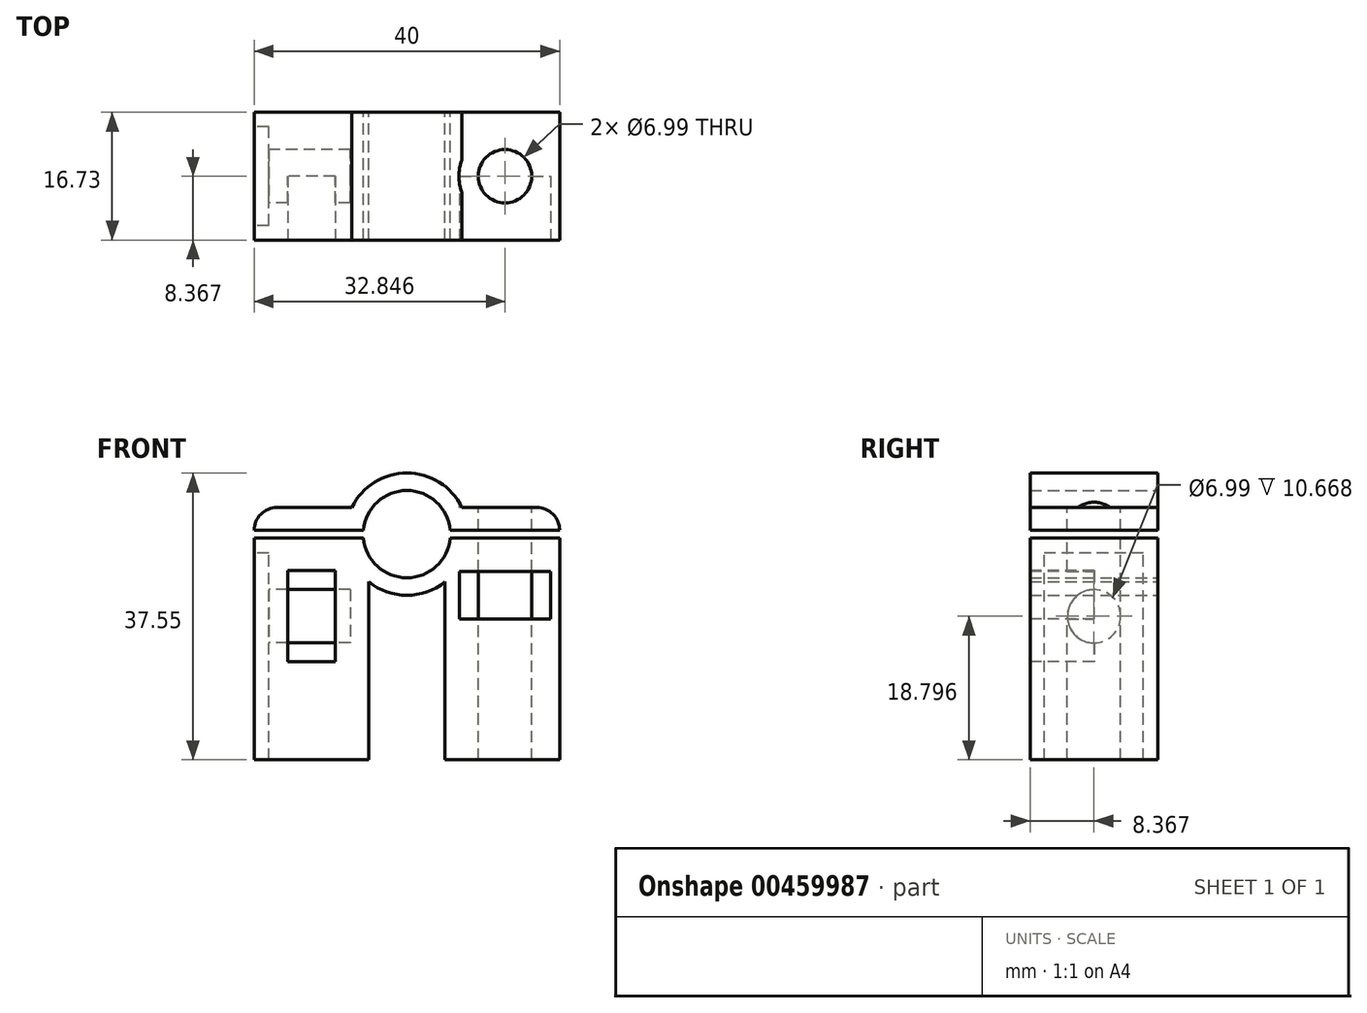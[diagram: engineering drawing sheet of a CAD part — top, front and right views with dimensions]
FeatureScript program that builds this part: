
annotation { "Feature Type Name" : "Feature", "Feature Type Description" : "" }
export const myFeature = defineFeature(function(context is Context, id is Id, definition is map)
    precondition{}
    {
        {
            var Q0;
            Q0=qCreatedBy(makeId("Front.planeOp"),FACE);
            var sketch = newSketch(context, id + "F0", { "sketchPlane" : qUnion([Q0])});
            skLineSegment(sketch, "E0.bottom", {"start": v(0, 0) * mm, "end": v(-40, 0) * mm, "construction": true});
            skLineSegment(sketch, "E0.top", {"start": v(0, 29.05) * mm, "end": v(-40, 29.05) * mm, "construction": true});
            skLineSegment(sketch, "E0.left", {"start": v(0, 0) * mm, "end": v(0, 29.05) * mm});
            skLineSegment(sketch, "E0.right", {"start": v(-40, 0) * mm, "end": v(-40, 29.05) * mm});
            skArc(sketch, "E1", {"start": v(-25.7, 29.05) * mm, "mid": v(-20, 23.84) * mm, "end": v(-14.3, 29.05) * mm});
            skLineSegment(sketch, "E2", {"start": v(-25.7, 29.05) * mm, "end": v(-40, 29.05) * mm});
            skLineSegment(sketch, "E3", {"start": v(-14.3, 29.05) * mm, "end": v(0, 29.05) * mm});
            skLineSegment(sketch, "E4.bottom", {"start": v(-40, 30.05) * mm, "end": v(0, 30.05) * mm, "construction": true});
            skArc(sketch, "E5", {"start": v(-14.3, 30.05) * mm, "mid": v(-20, 35.27) * mm, "end": v(-25.7, 30.05) * mm});
            skLineSegment(sketch, "E6", {"start": v(-40, 30.05) * mm, "end": v(-25.7, 30.05) * mm});
            skLineSegment(sketch, "E7", {"start": v(-14.3, 30.05) * mm, "end": v(0, 30.05) * mm});
            skLineSegment(sketch, "E8", {"start": v(-40, 30.05) * mm, "end": v(-40, 33.05) * mm});
            skLineSegment(sketch, "E9", {"start": v(-40, 33.05) * mm, "end": v(-27.2, 33.05) * mm});
            skLineSegment(sketch, "E10", {"start": v(0, 30.05) * mm, "end": v(0, 33.05) * mm});
            skLineSegment(sketch, "E11", {"start": v(0, 33.05) * mm, "end": v(-12.8, 33.05) * mm});
            skArc(sketch, "E12", {"start": v(-12.8, 33.05) * mm, "mid": v(-20, 37.55) * mm, "end": v(-27.2, 33.05) * mm});
            skArc(sketch, "E13", {"start": v(-25, 23.3) * mm, "mid": v(-20, 21.55) * mm, "end": v(-15, 23.3) * mm});
            skLineSegment(sketch, "E14", {"start": v(-25, 23.3) * mm, "end": v(-25, 0) * mm});
            skLineSegment(sketch, "E15", {"start": v(-15, 23.3) * mm, "end": v(-15, 0) * mm});
            skLineSegment(sketch, "E16", {"start": v(-25, 0) * mm, "end": v(-40, 0) * mm});
            skLineSegment(sketch, "E17", {"start": v(-15, 0) * mm, "end": v(0, 0) * mm});
            skSolve(sketch);
        }
        {
            var Q0;
            Q0 = qSketchRegion(id + "F0", true);
            extrude(context, id + "F1", {"entities" : qUnion([Q0]), "depth" : 12.73 * mm + 4 * mm});
        }
        {
            var Q0;
            Q0=makeQuery(id+"F1.opExtrude","SWEPT_FACE",FACE,{"disambiguationData":[OSD([sQuery(id+"F0.wireOp",EDGE,"E0.right")])]});
            var sketch = newSketch(context, id + "F2", { "sketchPlane" : qUnion([Q0])});
            skLineSegment(sketch, "E18.bottom", {"start": v(1.89, 0) * mm, "end": v(14.84, 0) * mm});
            skLineSegment(sketch, "E18.top", {"start": v(1.89, 27.05) * mm, "end": v(14.84, 27.05) * mm});
            skLineSegment(sketch, "E18.left", {"start": v(1.89, 0) * mm, "end": v(1.89, 27.05) * mm});
            skLineSegment(sketch, "E18.right", {"start": v(14.84, 0) * mm, "end": v(14.84, 27.05) * mm});
            skPoint(sketch, "E19", {"position": v(8.36, 27.05) * mm});
            skPoint(sketch, "E20", {"position": v(8.36, 29.05) * mm});
            skSolve(sketch);
        }
        {
            var Q0;
            Q0 = qSketchRegion(id + "F2", true);
            extrude(context, id + "F3", {"entities" : qUnion([Q0]), "operationType" : NewBodyOperationType.REMOVE, "oppositeDirection" : true, "depth" : 1.9 * mm});
        }
        {
            var Q0;
            Q0=makeQuery(id+"F3.boolean.opBoolean","COPY",FACE,{"derivedFrom":makeQuery(id+"F3.opExtrude","CAP_FACE",FACE,{"disambiguationData":[OSD([sQuery(id+"F2.wireOp",EDGE,"E18.bottom"),sQuery(id+"F2.wireOp",EDGE,"E18.top"),sQuery(id+"F2.wireOp",EDGE,"E18.left"),sQuery(id+"F2.wireOp",EDGE,"E18.right")])],"isStart":false})});
            var sketch = newSketch(context, id + "F4", { "sketchPlane" : qUnion([Q0])});
            skLineSegment(sketch, "E21", {"start": v(8.36, 0) * mm, "end": v(8.36, 27.05) * mm, "construction": true});
            skCircle(sketch, "E22", {"center": v(8.36, 18.8) * mm, "radius": 3.5 * mm});
            skSolve(sketch);
        }
        {
            var Q0;
            Q0 = qSketchRegion(id + "F4", true);
            extrude(context, id + "F5", {"entities" : qUnion([Q0]), "operationType" : NewBodyOperationType.REMOVE, "oppositeDirection" : true, "depth" : 10.67 * mm});
        }
        {
            var Q0;
            Q0=makeQuery(id+"F1.opExtrude","SWEPT_EDGE",EDGE,{"disambiguationData":[OSD([sQuery(id+"F0.wireOp",EDGE,"E8"),sQuery(id+"F0.wireOp",EDGE,"E9")])]});
            var Q1;
            Q1=makeQuery(id+"F1.opExtrude","SWEPT_EDGE",EDGE,{"disambiguationData":[OSD([sQuery(id+"F0.wireOp",EDGE,"E10"),sQuery(id+"F0.wireOp",EDGE,"E11")])]});
            fillet(context, id + "F6", {"entities" : qUnion([Q0, Q1]), "radius" : 3 * mm, "tangentPropagation" : true, "allowEdgeOverflow" : false});
        }
        {
            var Q0;
            Q0=makeQuery(id+"F1.opExtrude","SWEPT_FACE",FACE,{"disambiguationData":[OSD([sQuery(id+"F0.wireOp",EDGE,"E11")])]});
            var sketch = newSketch(context, id + "F7", { "sketchPlane" : qUnion([Q0])});
            skCircle(sketch, "E23", {"center": v(-7.15, -8.36) * mm, "radius": 3.5 * mm});
            skLineSegment(sketch, "E24", {"start": v(0, 0) * mm, "end": v(-14.3, 0) * mm, "construction": true});
            skPoint(sketch, "E25", {"position": v(-7.15, 0) * mm});
            skLineSegment(sketch, "E26", {"start": v(-7.15, 0) * mm, "end": v(-7.9, -16.73) * mm, "construction": true});
            skSolve(sketch);
        }
        {
            var Q0;
            Q0 = qSketchRegion(id + "F7", true);
            extrude(context, id + "F8", {"entities" : qUnion([Q0]), "operationType" : NewBodyOperationType.REMOVE, "endBound" : BoundingType.THROUGH_ALL, "oppositeDirection" : true, "depth" : 19.05 * mm});
        }
        {
            var Q0;
            Q0=makeQuery(id+"F1.opExtrude","SWEPT_FACE",FACE,{"disambiguationData":[OSD([sQuery(id+"F0.wireOp",EDGE,"E3")])]});
            var sketch = newSketch(context, id + "F9", { "sketchPlane" : qUnion([Q0])});
            skCircle(sketch, "E27", {"center": v(-7.15, -8.36) * mm, "radius": 3.5 * mm});
            skSolve(sketch);
        }
        {
            var Q0;
            Q0 = qSketchRegion(id + "F9", true);
            extrude(context, id + "F10", {"entities" : qUnion([Q0]), "operationType" : NewBodyOperationType.REMOVE, "oppositeDirection" : true, "depth" : 13 * mm});
        }
        {
            var Q0;
            Q0=makeQuery(id+"F1.opExtrude","CAP_FACE",FACE,{"disambiguationData":[OSD([sQuery(id+"F0.wireOp",EDGE,"E0.left"),sQuery(id+"F0.wireOp",EDGE,"E0.right"),sQuery(id+"F0.wireOp",EDGE,"E1"),sQuery(id+"F0.wireOp",EDGE,"E2"),sQuery(id+"F0.wireOp",EDGE,"E3"),sQuery(id+"F0.wireOp",EDGE,"E13"),sQuery(id+"F0.wireOp",EDGE,"E14"),sQuery(id+"F0.wireOp",EDGE,"E15"),sQuery(id+"F0.wireOp",EDGE,"E16"),sQuery(id+"F0.wireOp",EDGE,"E17")])],"isStart":false});
            var sketch = newSketch(context, id + "F11", { "sketchPlane" : qUnion([Q0])});
            skLineSegment(sketch, "E28.bottom", {"start": v(-35.61, 24.77) * mm, "end": v(-29.39, 24.77) * mm});
            skLineSegment(sketch, "E28.top", {"start": v(-35.61, 12.83) * mm, "end": v(-29.39, 12.83) * mm});
            skLineSegment(sketch, "E28.left", {"start": v(-35.61, 24.77) * mm, "end": v(-35.61, 12.83) * mm});
            skLineSegment(sketch, "E28.right", {"start": v(-29.39, 24.77) * mm, "end": v(-29.39, 12.83) * mm});
            skLineSegment(sketch, "E29.bottom", {"start": v(-13.12, 24.66) * mm, "end": v(-1.18, 24.66) * mm});
            skLineSegment(sketch, "E29.top", {"start": v(-13.12, 18.44) * mm, "end": v(-1.18, 18.44) * mm});
            skLineSegment(sketch, "E29.left", {"start": v(-13.12, 24.66) * mm, "end": v(-13.12, 18.44) * mm});
            skLineSegment(sketch, "E29.right", {"start": v(-1.18, 24.66) * mm, "end": v(-1.18, 18.44) * mm});
            skLineSegment(sketch, "E30", {"start": v(-40, 11.65) * mm, "end": v(-25, 11.65) * mm, "construction": true});
            skPoint(sketch, "E31", {"position": v(-32.5, 11.65) * mm});
            skPoint(sketch, "E32", {"position": v(-7.15, 18.44) * mm});
            skPoint(sketch, "E33", {"position": v(-32.5, 12.83) * mm});
            skPoint(sketch, "E34", {"position": v(-29.39, 18.8) * mm});
            skLineSegment(sketch, "E35", {"start": v(-35.61, 24.77) * mm, "end": v(-40, 24.77) * mm, "construction": true});
            skLineSegment(sketch, "E36", {"start": v(-1.18, 24.66) * mm, "end": v(-1.18, 29.05) * mm, "construction": true});
            skLineSegment(sketch, "E37", {"start": v(-14.3, 30.05) * mm, "end": v(-14.3, 0) * mm, "construction": true});
            skLineSegment(sketch, "E38", {"start": v(-14.3, 15.03) * mm, "end": v(0, 15.03) * mm, "construction": true});
            skPoint(sketch, "E39", {"position": v(-7.15, 15.03) * mm});
            skSolve(sketch);
        }
        {
            var Q0;
            Q0 = qSketchRegion(id + "F11", true);
            extrude(context, id + "F12", {"entities" : qUnion([Q0]), "operationType" : NewBodyOperationType.REMOVE, "oppositeDirection" : true, "depth" : 16.73 / 2 * mm + .45 / 50.8 * mm});
        }
        {
            var Q0;
            Q0=makeQuery(id+"F1.opExtrude","SWEPT_FACE",FACE,{"disambiguationData":[OSD([sQuery(id+"F0.wireOp",EDGE,"E11")])]});
            var sketch = newSketch(context, id + "F13", { "sketchPlane" : qUnion([Q0])});
            skCircle(sketch, "E40", {"center": v(-7.15, -8.36) * mm, "radius": 6.03 * mm});
            skSolve(sketch);
        }
        {
            var Q0;
            Q0 = qSketchRegion(id + "F13", true);
            extrude(context, id + "F14", {"entities" : qUnion([Q0]), "operationType" : NewBodyOperationType.REMOVE, "depth" : 25 * mm});
        }
    });
